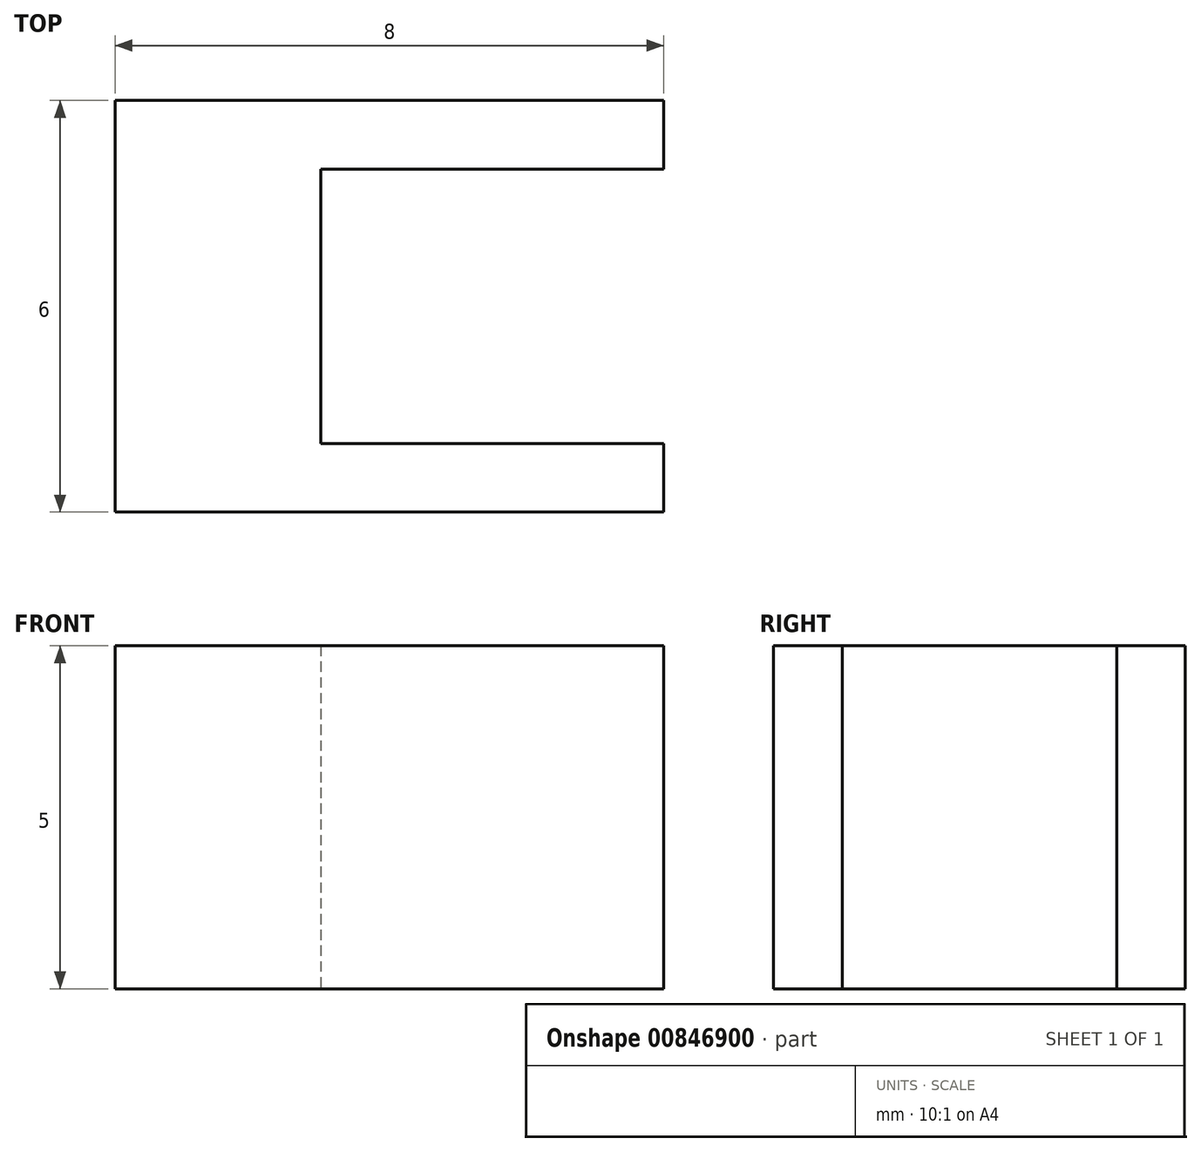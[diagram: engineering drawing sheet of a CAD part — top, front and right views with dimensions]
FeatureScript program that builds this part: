
annotation { "Feature Type Name" : "Feature", "Feature Type Description" : "" }
export const myFeature = defineFeature(function(context is Context, id is Id, definition is map)
    precondition{}
    {
        {
            var Q0;
            Q0=qCreatedBy(makeId("Top.planeOp"),FACE);
            var sketch = newSketch(context, id + "F0", { "sketchPlane" : qUnion([Q0])});
            skLineSegment(sketch, "E0.bottom", {"start": v(0, 0) * mm, "end": v(8, 0) * mm});
            skLineSegment(sketch, "E0.top", {"start": v(0, -6) * mm, "end": v(8, -6) * mm});
            skLineSegment(sketch, "E0.left", {"start": v(0, 0) * mm, "end": v(0, -6) * mm});
            skLineSegment(sketch, "E0.right", {"start": v(8, 0) * mm, "end": v(8, -6) * mm});
            skLineSegment(sketch, "E1.bottom", {"start": v(8, -1) * mm, "end": v(3, -1) * mm});
            skLineSegment(sketch, "E1.top", {"start": v(8, -5) * mm, "end": v(3, -5) * mm});
            skLineSegment(sketch, "E1.left", {"start": v(8, -1) * mm, "end": v(8, -5) * mm});
            skLineSegment(sketch, "E1.right", {"start": v(3, -1) * mm, "end": v(3, -5) * mm});
            skSolve(sketch);
        }
        {
            var Q0;
            {var subQ1=sQuery(id+"F0.wireOp",EDGE,"E0.bottom");Q0=makeQuery(id+"F0.imprint","IMPRINT",FACE,{"disambiguationData":[TD([[makeQuery(id+"F0.imprint","IMPRINT",EDGE,{"derivedFrom":subQ1}),-1.0]])]});}
            extrude(context, id + "F1", {"entities" : qUnion([Q0]), "depth" : 5 * mm, "offsetDistance" : 25 * mm});
        }
    });
